# Revit family: LEGRAND_TOMAS SIN ENCLAVAMIENTO_EMPOTRADAS_IP44_40
name_source: partatom
category: Installations électriques
revit_build: Autodesk Revit 2018 (Build: 20170223_1515(x64)
units: mm (PartAtom-declared; Revit-internal decimal feet)

## family parameters
Conserver l'orientation des annotations = Non
Cote de connecteur circulaire = Utiliser le diamètre
Couper avec des vides une fois chargée = Non
Hôte = Face
Partagée = Non
Point de calcul de pièce = Non
Type d'élément = Normal

## types (3) — shared parameters
Condiciones Generales de Uso = https://export.legrand.com
Description = Toma AL estándar internacional para montaje empotrado o en superficie con accesorio permite la alimentación de aparatos de potencia
Dia bouchon = 42 mm
Elévation par défaut = 1000 mm  [stored 3.28084 ft]
Estándar CEI o NFC = CEI
Fabricant = Legrand
RAY BOUCHON = 21 mm  [stored 0.0688976 ft]
Ray = 21 mm  [stored 0.0688976 ft]
Temperatura maxima de instalación = 40°C
Temperatura maxima de uso = 100°C
Temperatura minima de instalación = -20°C
Temperatura minima de uso = -50°C
Tension V = 40 50 V  50/60 Hz blanco
altura mm = 72 mm  [stored 0.23622 ft]
ancho mm = 64 mm  [stored 0.209974 ft]
clase de protección IP = IP44
color característico = blanco
distancia de fijación horizontal mm = 52 mm
distancia de fijación vertical mm = 60 mm
h1 = 43 mm
instalación de empotrar E o de superficie S = empotrar y superficie
intensidad A = 16 A
materia de la caja = plástico
profundidad mm = 80 mm
resistencia a los choques IK = 09
sin halogeno = Oui
tipo de conexión = conexión por tonillo

## per-type parameters (varying)
| type | Modèle | numero de polos | posición de la tierra h | profundidad de empotrar mm |
| base para cuadro Hypra   IP44   MBT 16 A   40/50V   2P   plast | 052403 | 2 | 12 | 33 mm |
| base para cuadro Hypra   IP44   MBT 16 A   40/50V   3P   plast | 052404 | 3 | 12 | 41 mm |
| base para cuadro Hypra   IP44   MBT 16 A   20/50 V continuo   2P   plast | 052405 | 2 | 10 | 33 mm |

note: [stored X ft] marks values corroborated as IEEE doubles in the binary element streams (Revit-internal decimal feet)
